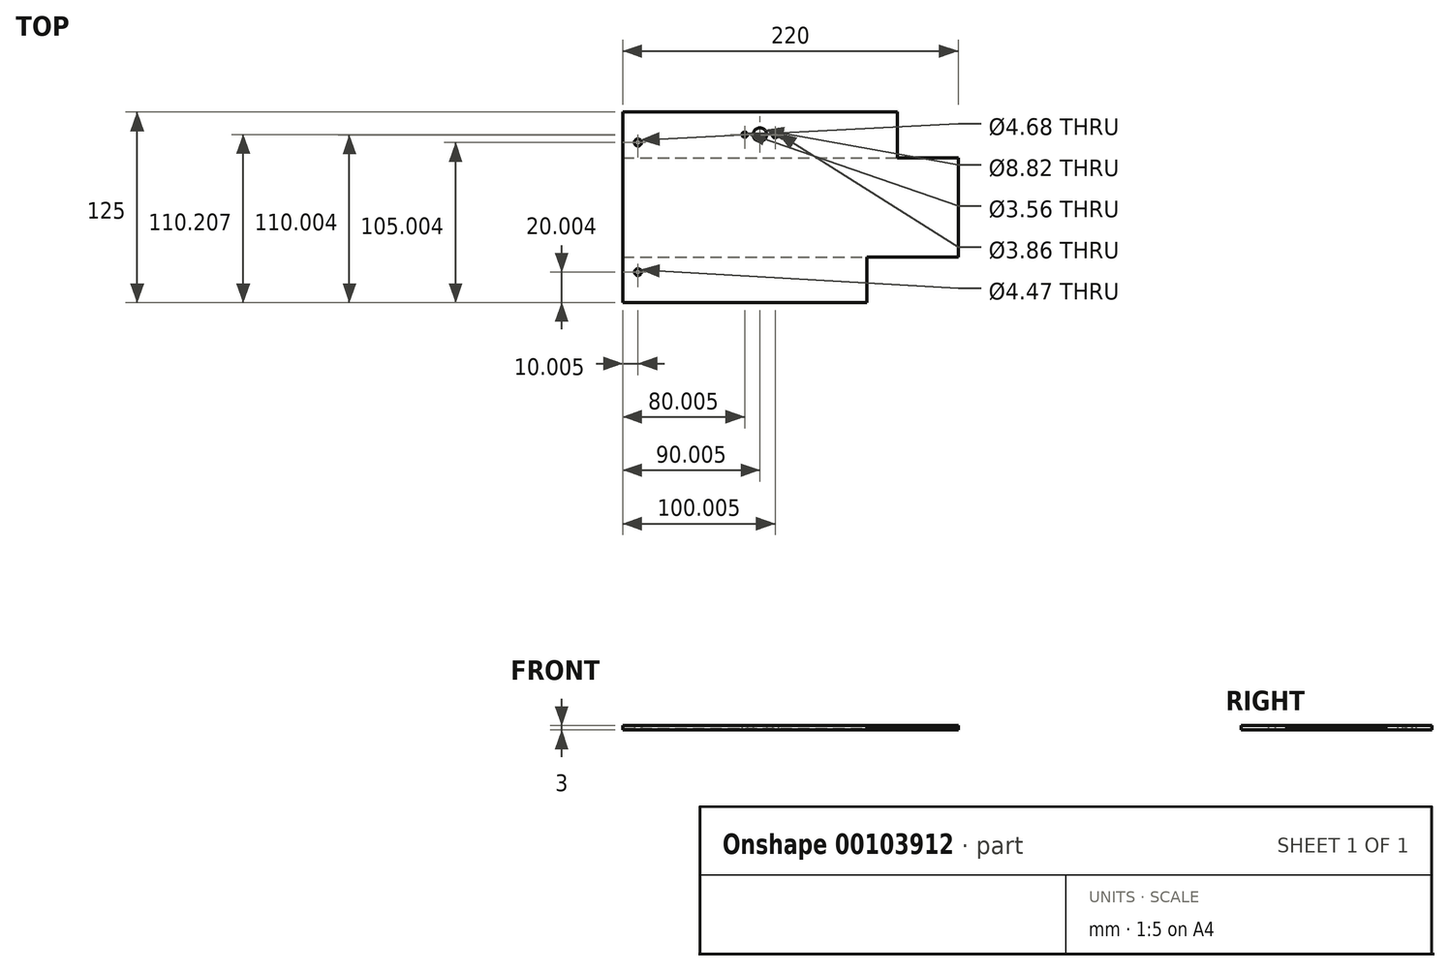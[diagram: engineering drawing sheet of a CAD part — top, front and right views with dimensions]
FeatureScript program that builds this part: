
annotation { "Feature Type Name" : "Feature", "Feature Type Description" : "" }
export const myFeature = defineFeature(function(context is Context, id is Id, definition is map)
    precondition{}
    {
        {
            var Q0;
            Q0=qCreatedBy(makeId("Top.planeOp"),FACE);
            var sketch = newSketch(context, id + "F0", { "sketchPlane" : qUnion([Q0])});
            skLineSegment(sketch, "E0.bottom", {"start": v(-90.43, 63.78) * mm, "end": v(89.57, 63.78) * mm});
            skLineSegment(sketch, "E0.top", {"start": v(-90.43, -61.22) * mm, "end": v(69.57, -61.22) * mm});
            skLineSegment(sketch, "E0.left", {"start": v(-90.43, 63.78) * mm, "end": v(-90.43, -61.22) * mm});
            skLineSegment(sketch, "E0.right", {"start": v(129.57, 33.78) * mm, "end": v(129.57, -31.22) * mm});
            skLineSegment(sketch, "E1", {"start": v(-90.43, -31.22) * mm, "end": v(129.57, -31.22) * mm});
            skLineSegment(sketch, "E2", {"start": v(-90.43, 33.78) * mm, "end": v(129.57, 33.78) * mm});
            skLineSegment(sketch, "E3", {"start": v(89.57, 33.78) * mm, "end": v(89.57, 63.78) * mm});
            skPoint(sketch, "E4.orphan", {"position": v(129.57, 63.78) * mm});
            skPoint(sketch, "E5.orphan", {"position": v(129.57, -61.22) * mm});
            skCircle(sketch, "E6", {"center": v(-80.43, -41.22) * mm, "radius": 2.23 * mm});
            skCircle(sketch, "E7", {"center": v(-80.43, 43.78) * mm, "radius": 2.34 * mm});
            skCircle(sketch, "E8", {"center": v(-0.43, 48.99) * mm, "radius": 4.41 * mm});
            skCircle(sketch, "E9", {"center": v(-10.43, 48.99) * mm, "radius": 1.78 * mm});
            skCircle(sketch, "E10", {"center": v(9.57, 48.78) * mm, "radius": 1.93 * mm});
            skLineSegment(sketch, "E11", {"start": v(69.57, -31.22) * mm, "end": v(69.57, -61.22) * mm});
            skPoint(sketch, "E12.orphan", {"position": v(89.57, -61.22) * mm});
            skSolve(sketch);
        }
        {
            var Q0;
            {var subQ1=sQuery(id+"F0.wireOp",EDGE,"E0.bottom");Q0=makeQuery(id+"F0.imprint","IMPRINT",FACE,{"disambiguationData":[TD([[makeQuery(id+"F0.imprint","IMPRINT",EDGE,{"derivedFrom":subQ1}),-1.0]])]});}
            var Q1;
            Q1=makeQuery(id+"F0.imprint","IMPRINT",FACE,{"disambiguationData":[TD([[makeQuery(id+"F0.imprint","IMPRINT",EDGE,{"derivedFrom":sQuery(id+"F0.wireOp",EDGE,"HDtrJbjU-ibVL-qtik-j0kB-dctEyZdCvw4N")}),-1.0]])]});
            var Q2;
            {var subQ5=sQuery(id+"F0.wireOp",EDGE,"E0.right");Q2=makeQuery(id+"F0.imprint","IMPRINT",FACE,{"disambiguationData":[TD([[makeQuery(id+"F0.imprint","IMPRINT",EDGE,{"derivedFrom":subQ5}),-1.0]])]});}
            var Q3;
            {var subQ1=sQuery(id+"F0.wireOp",EDGE,"E0.top");Q3=makeQuery(id+"F0.imprint","IMPRINT",FACE,{"disambiguationData":[TD([[makeQuery(id+"F0.imprint","IMPRINT",EDGE,{"derivedFrom":subQ1}),1.0]])]});}
            extrude(context, id + "F1", {"entities" : qUnion([Q0, Q1, Q2, Q3]), "depth" : 3 * mm});
        }
        {
            var Q0;
            {var subQ1=sQuery(id+"F0.wireOp",EDGE,"E0.left");var subQ5=sQuery(id+"F0.wireOp",EDGE,"E1");var subQ8=makeQuery(id+"F0.imprint","INTERSECT",VERTEX,{"derivedFrom":[subQ1,subQ5]});Q0=makeQuery(id+"F0.imprint","IMPRINT",FACE,{"disambiguationData":[TD([[makeQuery(id+"F0.imprint","IMPRINT",EDGE,{"disambiguationData":[TD([[subQ8,1.0]])],"derivedFrom":subQ1}),1.0]])]});}
            extrude(context, id + "F2", {"entities" : qUnion([Q0]), "depth" : 1 * mm});
        }
    });
